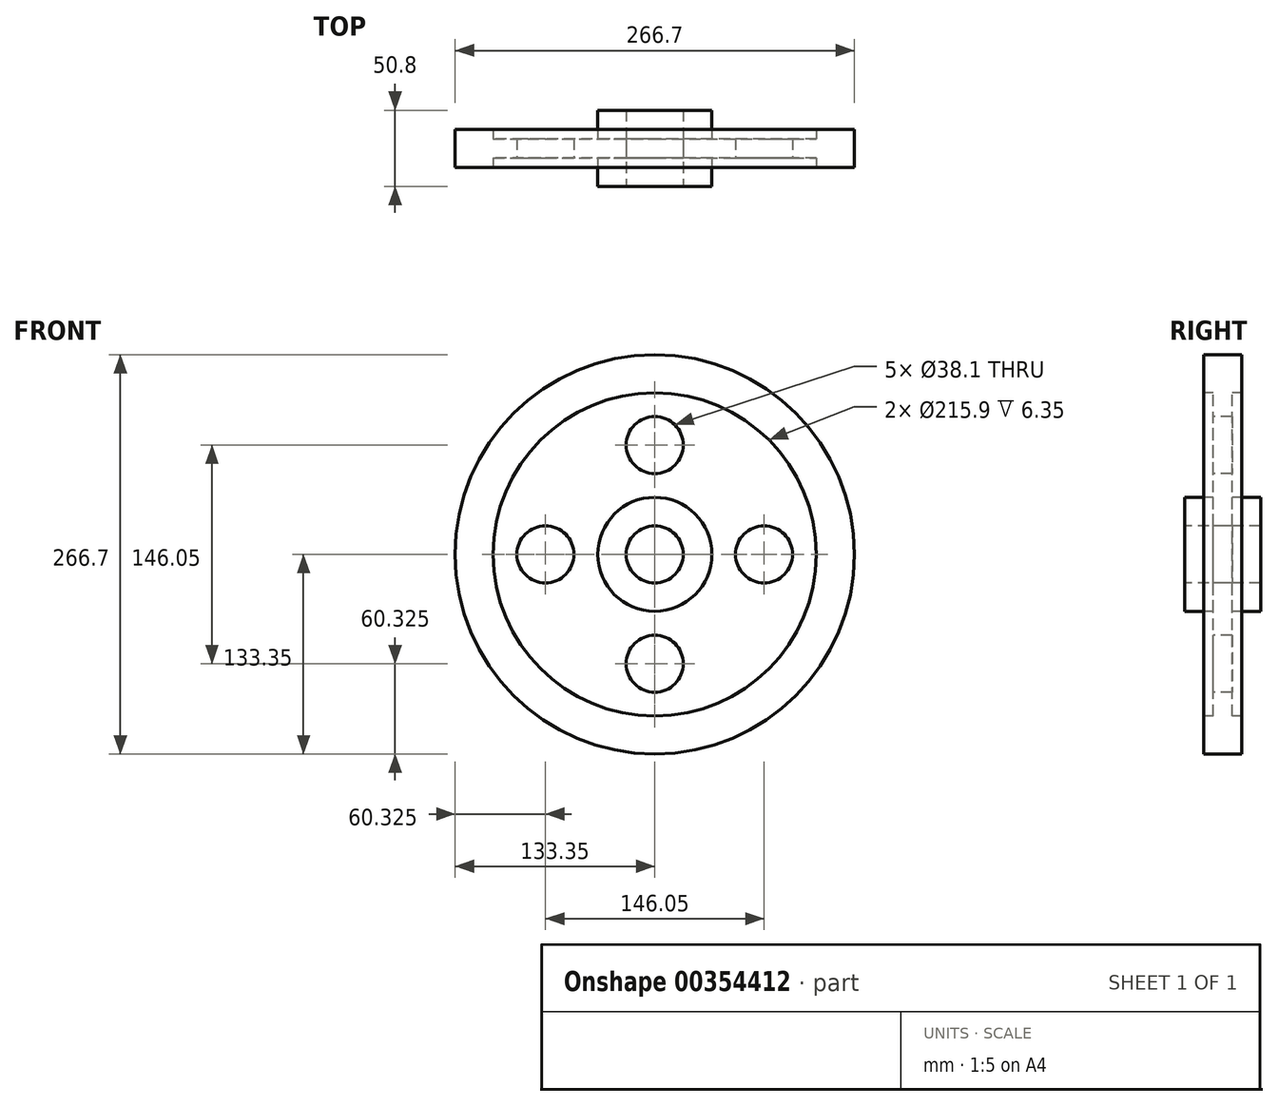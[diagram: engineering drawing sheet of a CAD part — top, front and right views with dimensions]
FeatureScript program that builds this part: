
annotation { "Feature Type Name" : "Feature", "Feature Type Description" : "" }
export const myFeature = defineFeature(function(context is Context, id is Id, definition is map)
    precondition{}
    {
        {
            var Q0;
            Q0=qCreatedBy(makeId("Right.planeOp"),FACE);
            var sketch = newSketch(context, id + "F0", { "sketchPlane" : qUnion([Q0])});
            skLineSegment(sketch, "E0", {"start": v(0, 0) * mm, "end": v(25.4, 0) * mm, "construction": true});
            skLineSegment(sketch, "E1.0", {"start": v(0, 19.05) * mm, "end": v(25.4, 19.05) * mm});
            skLineSegment(sketch, "E2.0", {"start": v(6.35, 38.1) * mm, "end": v(25.4, 38.1) * mm});
            skLineSegment(sketch, "E3.0", {"start": v(6.35, 107.95) * mm, "end": v(12.7, 107.95) * mm});
            skLineSegment(sketch, "E4.0", {"start": v(0, 133.35) * mm, "end": v(12.7, 133.35) * mm});
            skLineSegment(sketch, "E5", {"start": v(0, 133.35) * mm, "end": v(0, 0) * mm});
            skLineSegment(sketch, "E6.0", {"start": v(12.7, 133.35) * mm, "end": v(12.7, 107.95) * mm});
            skLineSegment(sketch, "E7.0", {"start": v(6.35, 107.95) * mm, "end": v(6.35, 38.1) * mm});
            skLineSegment(sketch, "E8.trimOffspring", {"start": v(25.4, 38.1) * mm, "end": v(25.4, 19.05) * mm});
            skLineSegment(sketch, "E9.MirrorCS", {"start": v(0, 133.35) * mm, "end": v(-12.7, 133.35) * mm});
            skLineSegment(sketch, "E10.MirrorCS", {"start": v(-12.7, 133.35) * mm, "end": v(-12.7, 107.95) * mm});
            skLineSegment(sketch, "E11.MirrorCS", {"start": v(-6.35, 107.95) * mm, "end": v(-6.35, 38.1) * mm});
            skLineSegment(sketch, "E12.MirrorCS", {"start": v(-6.35, 107.95) * mm, "end": v(-12.7, 107.95) * mm});
            skLineSegment(sketch, "E13.MirrorCS", {"start": v(-6.35, 38.1) * mm, "end": v(-25.4, 38.1) * mm});
            skLineSegment(sketch, "E14.MirrorCS", {"start": v(-25.4, 38.1) * mm, "end": v(-25.4, 19.05) * mm});
            skLineSegment(sketch, "E15.MirrorCS", {"start": v(0, 19.05) * mm, "end": v(-25.4, 19.05) * mm});
            skSolve(sketch);
        }
        {
            var Q0;
            {var subQ0=sQuery(id+"F0.wireOp",EDGE,"E9.MirrorCS");Q0=makeQuery(id+"F0.imprint","IMPRINT",FACE,{"disambiguationData":[TD([[makeQuery(id+"F0.imprint","IMPRINT",EDGE,{"derivedFrom":subQ0}),1.0]])]});}
            var Q1;
            {var subQ1=sQuery(id+"F0.wireOp",EDGE,"E1.0");Q1=makeQuery(id+"F0.imprint","IMPRINT",FACE,{"disambiguationData":[TD([[makeQuery(id+"F0.imprint","IMPRINT",EDGE,{"derivedFrom":subQ1}),1.0]])]});}
            var Q2;
            Q2=sQuery(id+"F0.wireOp",EDGE,"E0");
            revolve(context, id + "F1", {"entities" : qUnion([Q0, Q1]), "axis" : qUnion([Q2]), "revolveType" : RevolveType.FULL});
        }
        {
            var Q0;
            Q0=makeQuery(id+"F1.opRevolve","SWEPT_FACE",FACE,{"disambiguationData":[OSD([sQuery(id+"F0.wireOp",EDGE,"E11.MirrorCS")])]});
            var sketch = newSketch(context, id + "F2", { "sketchPlane" : qUnion([Q0])});
            skLineSegment(sketch, "E16", {"start": v(0, 0) * mm, "end": v(0, 73.03) * mm});
            skCircle(sketch, "E17", {"center": v(0, 73.03) * mm, "radius": 19.05 * mm});
            skCircle(sketch, "E18.1.0", {"center": v(-73.03, 0) * mm, "radius": 19.05 * mm});
            skCircle(sketch, "E18.2.0", {"center": v(0, -73.03) * mm, "radius": 19.05 * mm});
            skCircle(sketch, "E18.3.0", {"center": v(73.03, 0) * mm, "radius": 19.05 * mm});
            skPoint(sketch, "E18.center", {"position": v(0, 0) * mm});
            skSolve(sketch);
        }
        {
            var Q0;
            Q0=makeQuery(id+"F2.imprint","IMPRINT",FACE,{"disambiguationData":[TD([[makeQuery(id+"F2.imprint","IMPRINT",EDGE,{"derivedFrom":sQuery(id+"F2.wireOp",EDGE,"E18.3.0")}),1.0]])]});
            var Q1;
            Q1=makeQuery(id+"F2.imprint","IMPRINT",FACE,{"disambiguationData":[TD([[makeQuery(id+"F2.imprint","IMPRINT",EDGE,{"derivedFrom":sQuery(id+"F2.wireOp",EDGE,"E18.2.0")}),1.0]])]});
            var Q2;
            Q2=makeQuery(id+"F2.imprint","IMPRINT",FACE,{"disambiguationData":[TD([[makeQuery(id+"F2.imprint","IMPRINT",EDGE,{"derivedFrom":sQuery(id+"F2.wireOp",EDGE,"E18.1.0")}),1.0]])]});
            var Q3;
            Q3=makeQuery(id+"F2.imprint","IMPRINT",FACE,{"disambiguationData":[TD([[makeQuery(id+"F2.imprint","IMPRINT",EDGE,{"derivedFrom":sQuery(id+"F2.wireOp",EDGE,"E17")}),1.0]])]});
            extrude(context, id + "F3", {"entities" : qUnion([Q0, Q1, Q2, Q3]), "operationType" : NewBodyOperationType.REMOVE, "oppositeDirection" : true, "depth" : 25.4 * mm});
        }
    });
